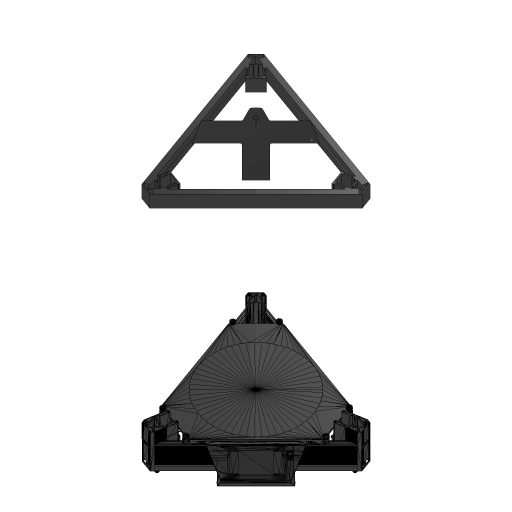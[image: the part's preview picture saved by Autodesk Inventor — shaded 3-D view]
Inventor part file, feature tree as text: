
AUTODESK INVENTOR PART (.ipt)
format: ipt  version: 2024.3 (Build 283343000, 343)  size: 65,220,096 bytes
history: native  units: mm
features: sketch x10, other x8, extrude x8, plane x2, pattern_circular x1, fillet x1, projected_geometry x1
ambient origin geometry x8: Origin, YZ Plane, XZ Plane, XY Plane, X Axis, Y Axis, Z Axis, Center Point
bodies: Body1 (feature_tree), Body2 (feature_tree), Body3 (feature_tree)
feature tree (31):
  other  "實體1"
  other  "Atom 3 lite bed"
  other  "修復的幾何圖形1"
  sketch  "草圖1"
  other  "移動本體1"
  plane  "工作平面1"
  extrude  "擠出1"  Depth=0.882617mm
  extrude  "擠出2"  Depth=0.003029mm
  pattern_circular  "環形陣列1"  [2 undecoded]
  sketch  "草圖4"
  plane  "工作平面2"
  extrude  "擠出3"  [1 undecoded]
  extrude  "擠出4"  TaperAngle=0.0deg  [1 undecoded]
  extrude  "擠出5"  Depth=400.0mm
  extrude  "擠出7"  Depth=32.5mm
  extrude  "擠出6"  Depth=14.0mm
  extrude  "擠出8"  Depth=700.0mm
  fillet  "圓角1"  Radius=2.0mm
  other  "工作軸線1"
  other  "MeshFeature1"
  sketch  "草圖2"
  sketch  "草圖3"
  other  "實體2"
  sketch  "草圖5"
  other  "實體3"
  sketch  "草圖6"
  projected_geometry  "投影迴路2"
  sketch  "草圖7"
  sketch  "草圖8"
  sketch  "草圖9"
  sketch  "草圖10"
note: 4 required parameter values undecoded (feature->parameter linkage not recoverable at this tier; creation-order binding heuristic only, values carry confidence <= 0.55)
